# Revit family: КШ РАШВОРК  арт.7015 .rfa
name_source: partatom
category: Арматура трубопроводов
units: mm (PartAtom-declared; Revit-internal decimal feet)

## family parameters
Всегда вертикально = Нет
На основе рабочей плоскости = Нет
Общий = Нет
При загрузке вырезать с полостями = Да
Размер круглого соединителя = Использовать диаметр
Тип детали = Нормальный

## types (8) — shared parameters
ADSK_Единица измерения = шт
ADSK_Завод-изготовитель = ООО "ТД "РАШВОРК"
B5 = 28 мм
URL = https://rwru.ru
Изготовитель = ООО "ТД "РАШВОРК"
Корпус = нерж. сталь CF8M
Ручка = нерж. сталь AISI304
Уго_длинна = 115 мм
zero-valued in all types: Отметка по умолчанию

## per-type parameters (varying)
- Кран шаровой полнопроходной РАШВОРК 7015 DN040 PN63, CF8M / AISI316 / PTFE, ВР/ВР, ISO 5211, рукоятка-рычаг, кв.14мм: A0=23 мм; A00=81 мм; A1=20 мм; A2=2 мм; A3=20 мм; A4=32 мм; A5=8 мм; ADSK_Код изделия=7015-040-63; ADSK_Масса=1.94; B1=64 мм; B2=73 мм; B3=13 мм; B4=6 мм; DN=38 мм; DN_соединителя=40 мм; H=109 мм; L=103 мм; LL=54 мм; TISO=6 мм; W=185 мм; А=36 мм; ВISO=70 мм; ВВ=69 мм; ШISO=70 мм; Шручки=25 мм
- Кран шаровой полнопроходной РАШВОРК 7015 DN008 PN63, CF8M / AISI316 / PTFE, ВР/ВР, ISO 5211, рукоятка-рычаг, кв.9мм: A0=12 мм; A00=41 мм; A1=11 мм; A2=1 мм; A3=10 мм; A4=13 мм; A5=6 мм; ADSK_Код изделия=7015-008-63; ADSK_Масса=0.37; B1=36 мм; B2=39 мм; B3=7 мм; B4=4 мм; DN=13 мм; DN_соединителя=9 мм; H=65 мм; L=56 мм; LL=22 мм; TISO=4 мм; W=115 мм; А=15 мм; ВISO=36 мм; ВВ=36 мм; ШISO=36 мм; Шручки=17 мм
- Кран шаровой полнопроходной РАШВОРК 7015 DN010 PN63, CF8M / AISI316 / PTFE, ВР/ВР, ISO 5211, рукоятка-рычаг, кв.9мм: A0=12 мм; A00=41 мм; A1=11 мм; A2=1 мм; A3=10 мм; A4=13 мм; A5=6 мм; ADSK_Код изделия=7015-010-63; ADSK_Масса=0.37; B1=36 мм; B2=39 мм; B3=7 мм; B4=4 мм; DN=13 мм; DN_соединителя=10 мм; H=65 мм; L=56 мм; LL=22 мм; TISO=4 мм; W=115 мм; А=15 мм; ВISO=36 мм; ВВ=36 мм; ШISO=36 мм; Шручки=17 мм
- Кран шаровой полнопроходной РАШВОРК 7015 DN015 PN63, CF8M / AISI316 / PTFE, ВР/ВР, ISO 5211, рукоятка-рычаг, кв.9мм: A0=12 мм; A00=46 мм; A1=12 мм; A2=1 мм; A3=12 мм; A4=15 мм; A5=7 мм; ADSK_Код изделия=7015-015-63; ADSK_Масса=0.37; B1=35 мм; B2=42 мм; B3=9 мм; B4=4 мм; DN=15 мм; DN_соединителя=15 мм; H=68 мм; L=59 мм; LL=25 мм; TISO=5 мм; W=140 мм; А=18 мм; ВISO=42 мм; ВВ=35 мм; ШISO=42 мм; Шручки=17 мм
- Кран шаровой полнопроходной РАШВОРК 7015 DN020 PN63, CF8M / AISI316 / PTFE, ВР/ВР, ISO 5211, рукоятка-рычаг, кв.9мм: A0=17 мм; A00=54 мм; A1=14 мм; A2=1 мм; A3=14 мм; A4=19 мм; A5=4 мм; ADSK_Код изделия=7015-020-63; ADSK_Масса=0.49; B1=39 мм; B2=47 мм; B3=9 мм; B4=4 мм; DN=20 мм; DN_соединителя=20 мм; H=73 мм; L=67 мм; LL=32 мм; TISO=5 мм; W=140 мм; А=21 мм; ВISO=42 мм; ВВ=44 мм; ШISO=42 мм; Шручки=19 мм
- Кран шаровой полнопроходной РАШВОРК 7015 DN025 PN63, CF8M / AISI316 / PTFE, ВР/ВР, ISO 5211, рукоятка-рычаг, кв.11мм: A0=21 мм; A00=64 мм; A1=15 мм; A2=1 мм; A3=19 мм; A4=23 мм; A5=3 мм; ADSK_Код изделия=7015-025-63; ADSK_Масса=0.74; B1=49 мм; B2=52 мм; B3=10 мм; B4=5 мм; DN=25 мм; DN_соединителя=25 мм; H=87 мм; L=80 мм; LL=39 мм; TISO=6 мм; W=160 мм; А=25 мм; ВISO=50 мм; ВВ=49 мм; ШISO=50 мм; Шручки=22 мм
- Кран шаровой полнопроходной РАШВОРК 7015 DN032 PN63, CF8M / AISI316 / PTFE, ВР/ВР, ISO 5211, рукоятка-рычаг, кв.11мм: A0=22 мм; A00=73 мм; A1=18 мм; A2=1 мм; A3=19 мм; A4=29 мм; A5=9 мм; ADSK_Код изделия=7015-032-63; ADSK_Масса=1.18; B1=62 мм; B2=65 мм; B3=10 мм; B4=5 мм; DN=32 мм; DN_соединителя=32 мм; H=100 мм; L=95 мм; LL=49 мм; TISO=6 мм; W=160 мм; А=31 мм; ВISO=50 мм; ВВ=62 мм; ШISO=50 мм; Шручки=22 мм
- Кран шаровой полнопроходной РАШВОРК 7015 DN050 PN63, CF8M / AISI316 / PTFE, ВР/ВР, ISO 5211, рукоятка-рычаг, кв.14мм: A0=28 мм; A00=99 мм; A1=22 мм; A2=2 мм; A3=29 мм; A4=39 мм; A5=10 мм; ADSK_Код изделия=7015-050-63; ADSK_Масса=2.9; B1=73 мм; B2=83 мм; B3=13 мм; B4=6 мм; DN=50 мм; DN_соединителя=50 мм; H=119 мм; L=125 мм; LL=67 мм; TISO=6 мм; W=185 мм; А=45 мм; ВISO=70 мм; ВВ=79 мм; ШISO=70 мм; Шручки=25 мм

note: column(s) folded — value = type name in every type: ADSK_Наименование
